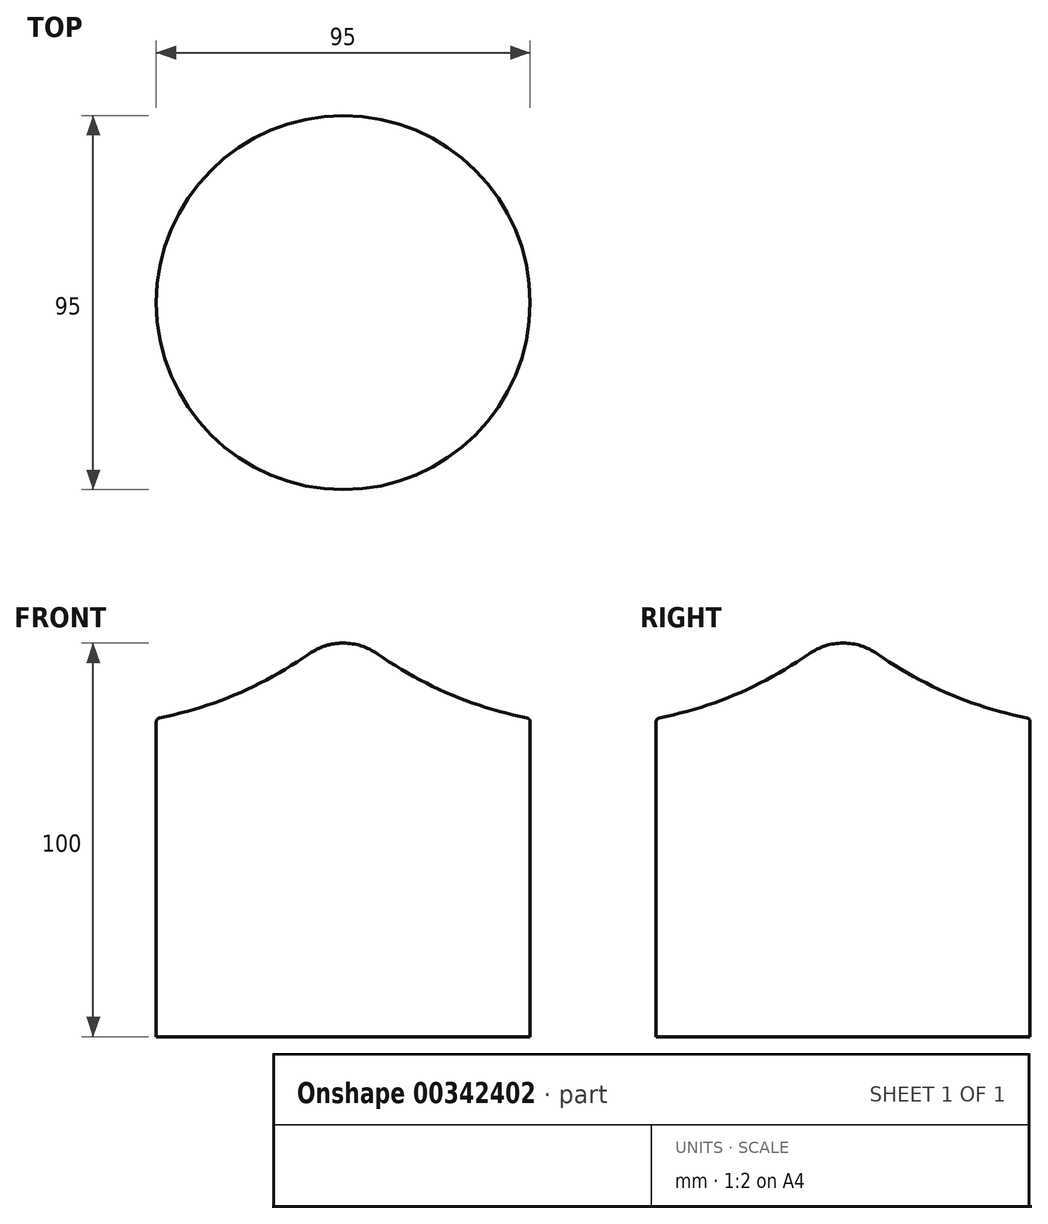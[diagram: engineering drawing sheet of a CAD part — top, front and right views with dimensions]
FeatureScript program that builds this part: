
annotation { "Feature Type Name" : "Feature", "Feature Type Description" : "" }
export const myFeature = defineFeature(function(context is Context, id is Id, definition is map)
    precondition{}
    {
        {
            var Q0;
            Q0=qCreatedBy(makeId("Front.planeOp"),FACE);
            var sketch = newSketch(context, id + "F0", { "sketchPlane" : qUnion([Q0])});
            skLineSegment(sketch, "E0", {"start": v(0, 0) * mm, "end": v(0, 100) * mm});
            skArc(sketch, "E1", {"start": v(0, 100) * mm, "mid": v(-4.56, 99.3) * mm, "end": v(-8.69, 97.26) * mm});
            skArc(sketch, "E2", {"start": v(-46.7, 80.98) * mm, "mid": v(-26.85, 87.15) * mm, "end": v(-8.69, 97.26) * mm});
            skArc(sketch, "E3", {"start": v(-46.7, 80.98) * mm, "mid": v(-47.27, 80.63) * mm, "end": v(-47.5, 80) * mm});
            skLineSegment(sketch, "E4", {"start": v(-47.5, 80) * mm, "end": v(-47.5, 0) * mm});
            skLineSegment(sketch, "E5", {"start": v(-47.5, 0) * mm, "end": v(0, 0) * mm});
            skSolve(sketch);
        }
        {
            var Q0;
            Q0=makeQuery(id+"F0.imprint","IMPRINT",FACE,{"disambiguationData":[TD([[makeQuery(id+"F0.imprint","IMPRINT",EDGE,{"derivedFrom":sQuery(id+"F0.wireOp",EDGE,"E0")}),1.0]])]});
            var Q1;
            Q1=sQuery(id+"F0.wireOp",EDGE,"E0");
            revolve(context, id + "F1", {"entities" : qUnion([Q0]), "axis" : qUnion([Q1]), "revolveType" : RevolveType.FULL});
        }
    });
